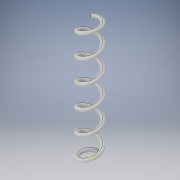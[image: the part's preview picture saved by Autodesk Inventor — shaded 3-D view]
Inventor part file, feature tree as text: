
AUTODESK INVENTOR PART (.ipt)
format: ipt  version: 2019 (Build 230136000, 136)  size: 427,520 bytes
history: native  units: in
note: dims shown in document units (in); Inventor stores cm internally (conversion verified against a paired STEP export)
features: other x7, sketch x2, helix x1
ambient origin geometry x8: Origin, YZ Plane, XZ Plane, XY Plane, X Axis, Y Axis, Z Axis, Center Point
bodies: Body1 (feature_tree)
feature tree (10):
  other  "Table"
  other  "Member = Part1-01"
  other  "Member = Part1-02"
  other  "Member = Part1-03"
  other  "Member = Part1-04"
  other  "Member = Part1-05"
  other  "Member = Part1-06"
  sketch  "Sketch2"  dims[d14=2.5in]
  sketch  "Sketch3"  dims[d16=0.0in d17=0.6871in d18=0.6871in d19=0.6871in d20=0.6871in]
  helix  "Coil2"  [1 undecoded]
note: 1 required parameter value undecoded (feature->parameter linkage not recoverable at this tier; creation-order binding heuristic only, values carry confidence <= 0.55)
